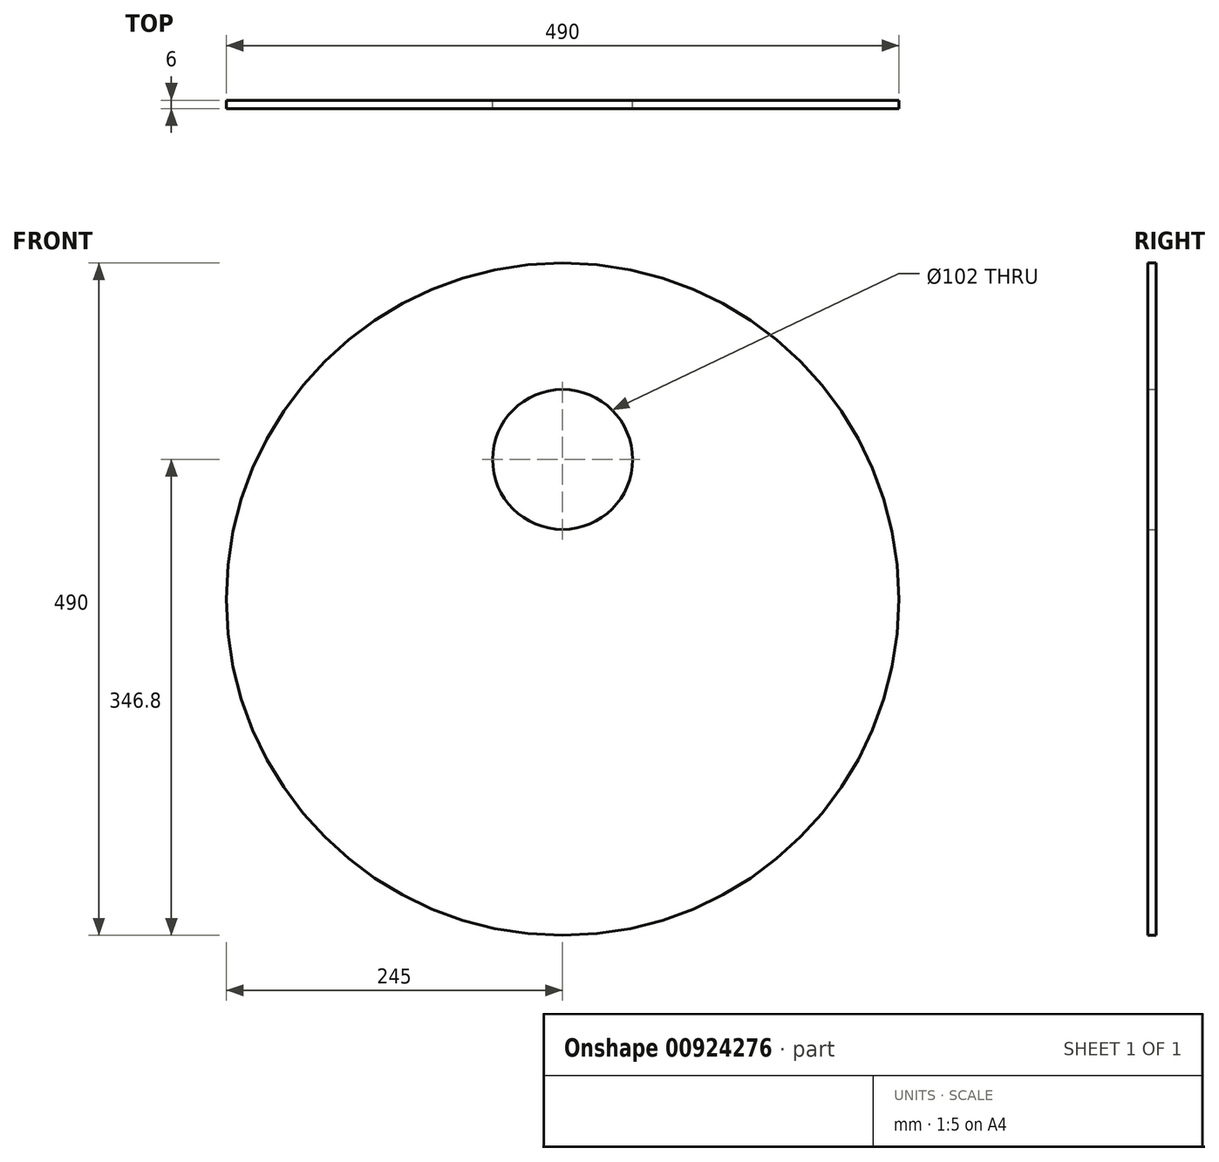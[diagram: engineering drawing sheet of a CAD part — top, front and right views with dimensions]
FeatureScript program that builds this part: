
annotation { "Feature Type Name" : "Feature", "Feature Type Description" : "" }
export const myFeature = defineFeature(function(context is Context, id is Id, definition is map)
    precondition{}
    {
        {
            var Q0;
            Q0=qCreatedBy(makeId("Front.planeOp"),FACE);
            var sketch = newSketch(context, id + "F0", { "sketchPlane" : qUnion([Q0])});
            skCircle(sketch, "E0", {"center": v(0, 0) * mm, "radius": 245 * mm});
            skCircle(sketch, "E1", {"center": v(0, 101.8) * mm, "radius": 51 * mm});
            skSolve(sketch);
        }
        {
            var Q0;
            Q0=makeQuery(id+"F0.imprint","IMPRINT",FACE,{"disambiguationData":[TD([[makeQuery(id+"F0.imprint","IMPRINT",EDGE,{"derivedFrom":sQuery(id+"F0.wireOp",EDGE,"E0")}),1.0]])]});
            extrude(context, id + "F1", {"entities" : qUnion([Q0]), "depth" : 6 * mm, "offsetDistance" : 25.4 * mm});
        }
    });
